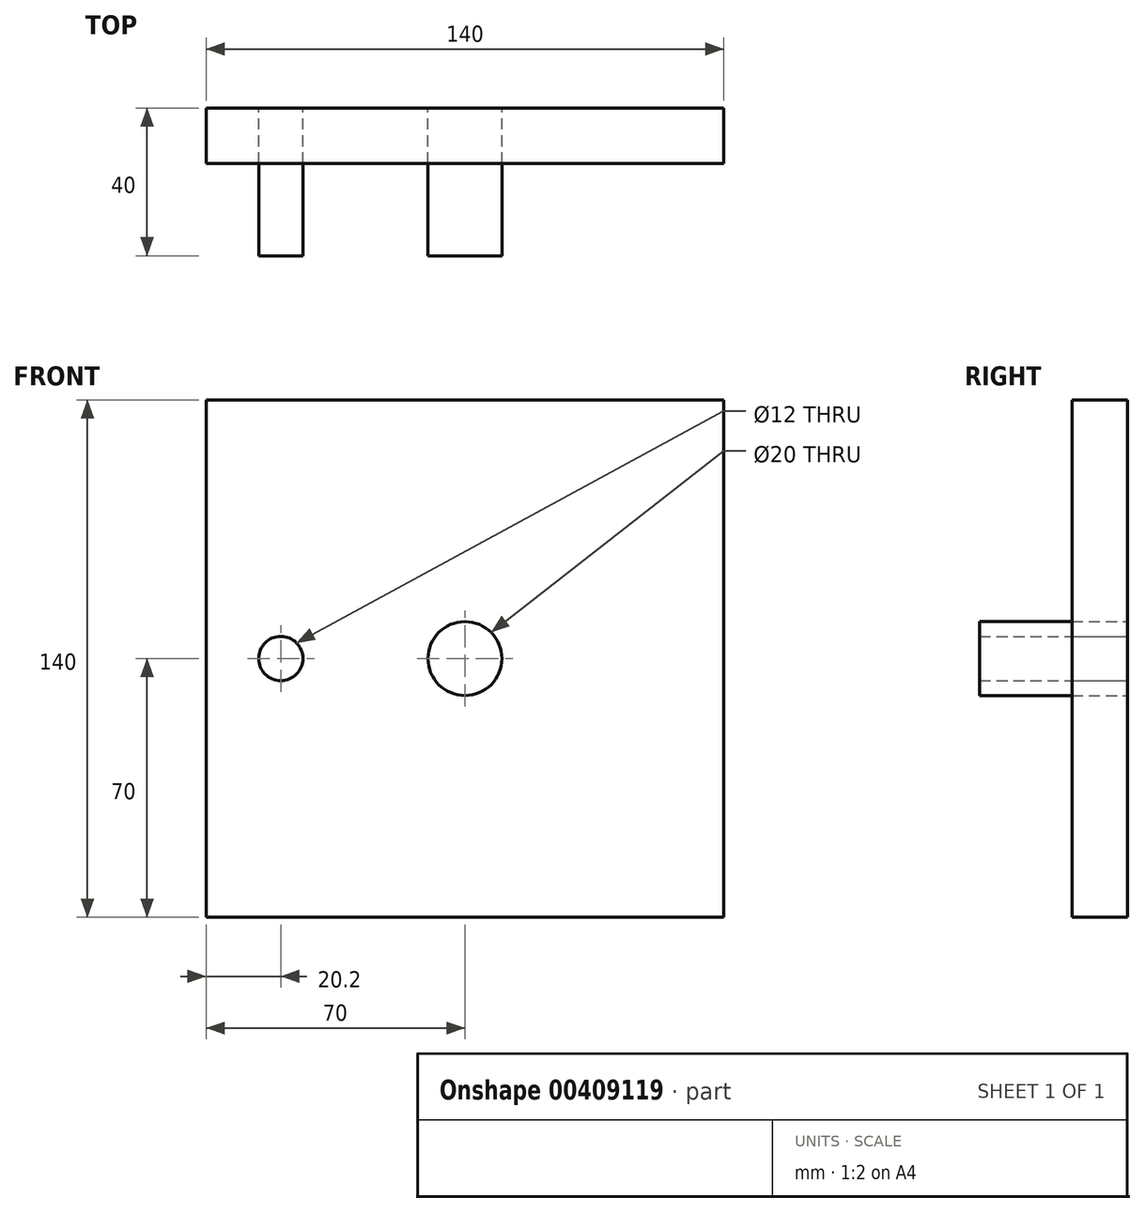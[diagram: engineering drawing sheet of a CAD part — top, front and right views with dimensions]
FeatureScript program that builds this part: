
annotation { "Feature Type Name" : "Feature", "Feature Type Description" : "" }
export const myFeature = defineFeature(function(context is Context, id is Id, definition is map)
    precondition{}
    {
        {
            var Q0;
            Q0=qCreatedBy(makeId("Front.planeOp"),FACE);
            var sketch = newSketch(context, id + "F0", { "sketchPlane" : qUnion([Q0])});
            skCircle(sketch, "E0", {"center": v(-49.8, 0) * mm, "radius": 6 * mm});
            skCircle(sketch, "E1", {"center": v(0, 0) * mm, "radius": 10 * mm});
            skLineSegment(sketch, "E2.bottom", {"start": v(-70, -70) * mm, "end": v(70, -70) * mm});
            skLineSegment(sketch, "E2.top", {"start": v(-70, 70) * mm, "end": v(70, 70) * mm});
            skLineSegment(sketch, "E2.left", {"start": v(-70, -70) * mm, "end": v(-70, 70) * mm});
            skLineSegment(sketch, "E2.right", {"start": v(70, -70) * mm, "end": v(70, 70) * mm});
            skSolve(sketch);
        }
        {
            var Q0;
            Q0=makeQuery(id+"F0.imprint","IMPRINT",FACE,{"disambiguationData":[TD([[makeQuery(id+"F0.imprint","IMPRINT",EDGE,{"derivedFrom":sQuery(id+"F0.wireOp",EDGE,"E0")}),1.0]])]});
            var Q1;
            Q1=makeQuery(id+"F0.imprint","IMPRINT",FACE,{"disambiguationData":[TD([[makeQuery(id+"F0.imprint","IMPRINT",EDGE,{"derivedFrom":sQuery(id+"F0.wireOp",EDGE,"E1")}),1.0]])]});
            extrude(context, id + "F1", {"entities" : qUnion([Q0, Q1]), "depth" : 40 * mm});
        }
        {
            var Q0;
            Q0 = qSketchRegion(id + "F0", true);
            extrude(context, id + "F2", {"entities" : qUnion([Q0]), "depth" : 15 * mm});
        }
    });
